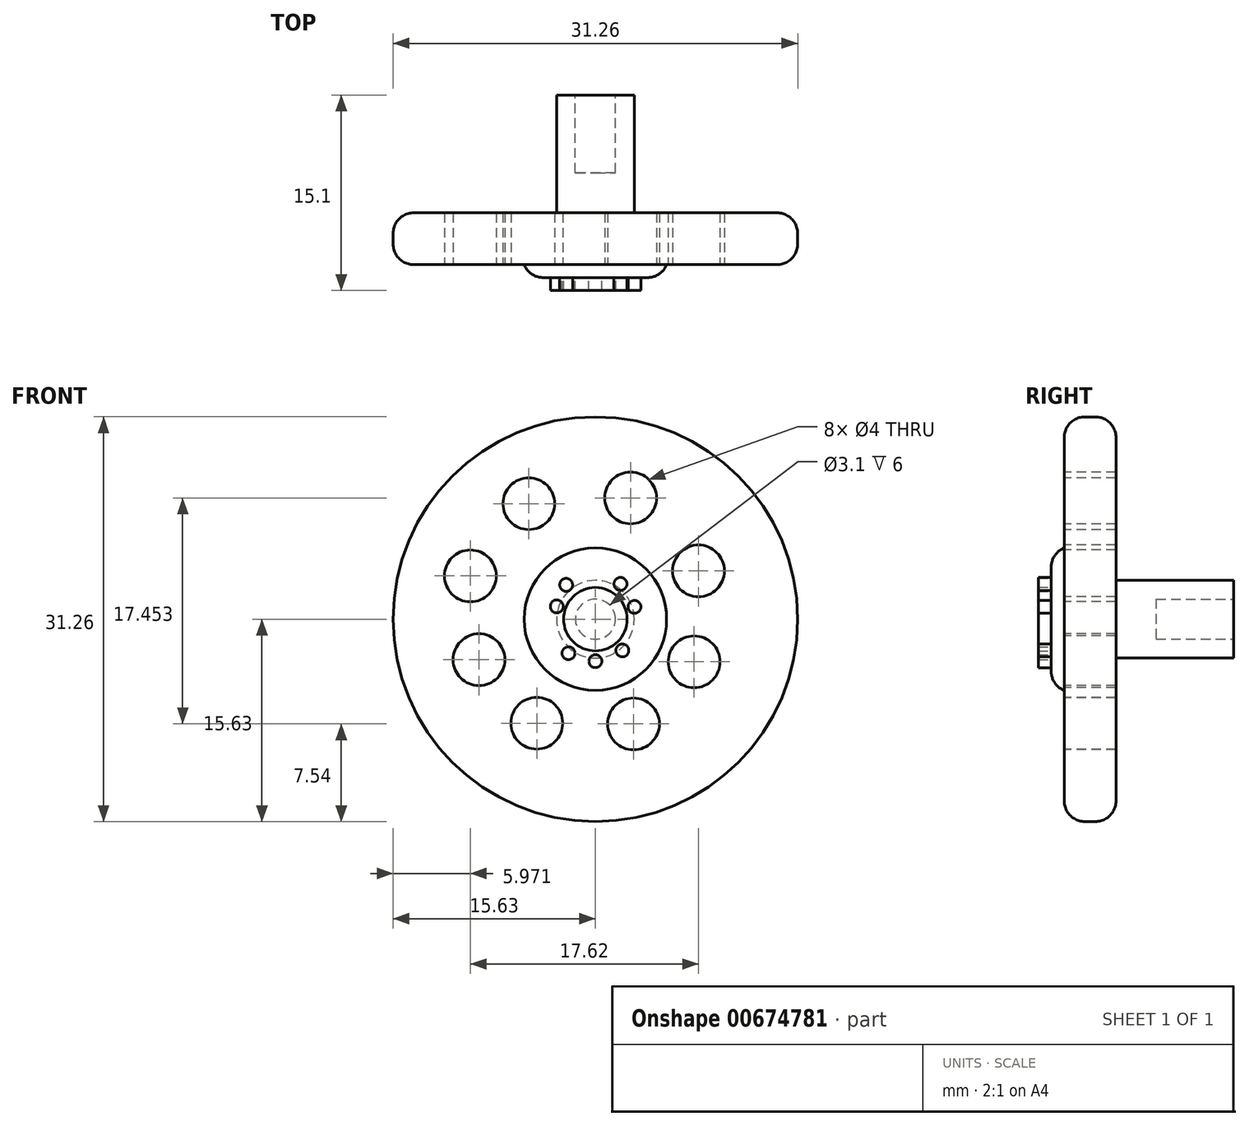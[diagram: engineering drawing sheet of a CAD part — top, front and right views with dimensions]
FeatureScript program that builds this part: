
annotation { "Feature Type Name" : "Feature", "Feature Type Description" : "" }
export const myFeature = defineFeature(function(context is Context, id is Id, definition is map)
    precondition{}
    {
        {
            var Q0;
            Q0=qCreatedBy(makeId("Front.planeOp"),FACE);
            var sketch = newSketch(context, id + "F0", { "sketchPlane" : qUnion([Q0])});
            skCircle(sketch, "E0", {"center": v(0, 0) * mm, "radius": 15.62 * mm});
            skSolve(sketch);
        }
        {
            var Q0;
            Q0=makeQuery(id+"F0.imprint","IMPRINT",FACE,{"disambiguationData":[TD([[makeQuery(id+"F0.imprint","IMPRINT",EDGE,{"derivedFrom":sQuery(id+"F0.wireOp",EDGE,"E0")}),1.0]])]});
            extrude(context, id + "F1", {"entities" : qUnion([Q0]), "depth" : 4 * mm, "offsetDistance" : 25.4 * mm});
        }
        {
            var Q0;
            Q0=makeQuery(id+"F1.opExtrude","CAP_FACE",FACE,{"disambiguationData":[OSD([sQuery(id+"F0.wireOp",EDGE,"E0")])],"isStart":false});
            var sketch = newSketch(context, id + "F2", { "sketchPlane" : qUnion([Q0])});
            skCircle(sketch, "E1", {"center": v(0, 0) * mm, "radius": 2.45 * mm});
            skSolve(sketch);
        }
        {
            var Q0;
            Q0=makeQuery(id+"F2.imprint","IMPRINT",FACE,{"disambiguationData":[TD([[makeQuery(id+"F2.imprint","IMPRINT",EDGE,{"derivedFrom":sQuery(id+"F2.wireOp",EDGE,"E1")}),1.0]])]});
            extrude(context, id + "F3", {"entities" : qUnion([Q0]), "operationType" : NewBodyOperationType.ADD, "depth" : 2 * mm, "offsetDistance" : 25.4 * mm});
        }
        {
            var Q0;
            Q0=makeQuery(id+"F1.opExtrude","CAP_FACE",FACE,{"disambiguationData":[OSD([sQuery(id+"F0.wireOp",EDGE,"E0")])],"isStart":true});
            var sketch = newSketch(context, id + "F4", { "sketchPlane" : qUnion([Q0])});
            skCircle(sketch, "E2", {"center": v(0, 0) * mm, "radius": 3 * mm});
            skSolve(sketch);
        }
        {
            var Q0;
            Q0 = qSketchRegion(id + "F4", true);
            extrude(context, id + "F5", {"entities" : qUnion([Q0]), "operationType" : NewBodyOperationType.ADD, "depth" : 9.1 * mm, "offsetDistance" : 25.4 * mm});
        }
        {
            var Q0;
            Q0=makeQuery(id+"F5.opExtrude","CAP_FACE",FACE,{"disambiguationData":[OSD([sQuery(id+"F4.wireOp",EDGE,"E2")])],"isStart":false});
            var sketch = newSketch(context, id + "F6", { "sketchPlane" : qUnion([Q0])});
            skCircle(sketch, "E3", {"center": v(0, 0) * mm, "radius": 1.55 * mm});
            skSolve(sketch);
        }
        {
            var Q0;
            Q0=makeQuery(id+"F6.imprint","IMPRINT",FACE,{"disambiguationData":[TD([[makeQuery(id+"F6.imprint","IMPRINT",EDGE,{"derivedFrom":sQuery(id+"F6.wireOp",EDGE,"E3")}),1.0]])]});
            extrude(context, id + "F7", {"entities" : qUnion([Q0]), "operationType" : NewBodyOperationType.REMOVE, "oppositeDirection" : true, "depth" : 6 * mm, "offsetDistance" : 25.4 * mm});
        }
        {
            var Q0;
            Q0=makeQuery(id+"F1.opExtrude","CAP_FACE",FACE,{"disambiguationData":[OSD([sQuery(id+"F0.wireOp",EDGE,"E0")])],"isStart":false});
            var sketch = newSketch(context, id + "F8", { "sketchPlane" : qUnion([Q0])});
            skCircle(sketch, "E4", {"center": v(0, 0) * mm, "radius": 5.5 * mm});
            skSolve(sketch);
        }
        {
            var Q0;
            Q0 = qSketchRegion(id + "F8", true);
            extrude(context, id + "F9", {"entities" : qUnion([Q0]), "operationType" : NewBodyOperationType.ADD, "depth" : 1 * mm, "offsetDistance" : 25.4 * mm});
        }
        {
            var Q0;
            Q0=makeQuery(id+"F1.opExtrude","CAP_EDGE",EDGE,{"disambiguationData":[OSD([sQuery(id+"F0.wireOp",EDGE,"E0")])],"isStart":false});
            var Q1;
            Q1=makeQuery(id+"F1.opExtrude","CAP_EDGE",EDGE,{"disambiguationData":[OSD([sQuery(id+"F0.wireOp",EDGE,"E0")])],"isStart":true});
            var Q2;
            Q2=makeQuery(id+"F9.opExtrude","CAP_EDGE",EDGE,{"disambiguationData":[OSD([sQuery(id+"F8.wireOp",EDGE,"E4")])],"isStart":false});
            fillet(context, id + "F10", {"entities" : qUnion([Q0, Q1, Q2]), "radius" : 1.59 * mm, "tangentPropagation" : true, "allowEdgeOverflow" : false});
        }
        {
            var Q0;
            Q0=makeQuery(id+"F9.opExtrude","CAP_FACE",FACE,{"disambiguationData":[OSD([sQuery(id+"F8.wireOp",EDGE,"E4")])],"isStart":false});
            var sketch = newSketch(context, id + "F11", { "sketchPlane" : qUnion([Q0])});
            skCircle(sketch, "E5", {"center": v(0, 3.12) * mm, "radius": 0.5 * mm});
            skCircle(sketch, "E6", {"center": v(-2.26, 2.65) * mm, "radius": 0.5 * mm});
            skCircle(sketch, "E7", {"center": v(-2.98, 0.99) * mm, "radius": 0.5 * mm});
            skCircle(sketch, "E8", {"center": v(1.94, 2.72) * mm, "radius": 0.5 * mm});
            skCircle(sketch, "E9", {"center": v(3.02, 0.95) * mm, "radius": 0.5 * mm});
            skCircle(sketch, "E10", {"center": v(-3.2, -0.9) * mm, "radius": 0.5 * mm});
            skCircle(sketch, "E11", {"center": v(3.02, -0.9) * mm, "radius": 0.5 * mm});
            skCircle(sketch, "E12", {"center": v(2.08, -2.41) * mm, "radius": 0.5 * mm});
            skCircle(sketch, "E13", {"center": v(-2.08, -2.63) * mm, "radius": 0.5 * mm});
            skCircle(sketch, "E14", {"center": v(0, -3.24) * mm, "radius": 0.5 * mm});
            skSolve(sketch);
        }
        {
            var Q0;
            Q0=makeQuery(id+"F11.imprint","IMPRINT",FACE,{"disambiguationData":[TD([[makeQuery(id+"F11.imprint","IMPRINT",EDGE,{"derivedFrom":sQuery(id+"F11.wireOp",EDGE,"E7")}),1.0]])]});
            var Q1;
            Q1=makeQuery(id+"F11.imprint","IMPRINT",FACE,{"disambiguationData":[TD([[makeQuery(id+"F11.imprint","IMPRINT",EDGE,{"derivedFrom":sQuery(id+"F11.wireOp",EDGE,"E6")}),1.0]])]});
            var Q2;
            Q2=makeQuery(id+"F11.imprint","IMPRINT",FACE,{"disambiguationData":[TD([[makeQuery(id+"F11.imprint","IMPRINT",EDGE,{"derivedFrom":sQuery(id+"F11.wireOp",EDGE,"E8")}),1.0]])]});
            var Q3;
            Q3=makeQuery(id+"F11.imprint","IMPRINT",FACE,{"disambiguationData":[TD([[makeQuery(id+"F11.imprint","IMPRINT",EDGE,{"derivedFrom":sQuery(id+"F11.wireOp",EDGE,"E9")}),1.0]])]});
            var Q4;
            Q4=makeQuery(id+"F11.imprint","IMPRINT",FACE,{"disambiguationData":[TD([[makeQuery(id+"F11.imprint","IMPRINT",EDGE,{"derivedFrom":sQuery(id+"F11.wireOp",EDGE,"E12")}),1.0]])]});
            var Q5;
            Q5=makeQuery(id+"F11.imprint","IMPRINT",FACE,{"disambiguationData":[TD([[makeQuery(id+"F11.imprint","IMPRINT",EDGE,{"derivedFrom":sQuery(id+"F11.wireOp",EDGE,"E14")}),1.0]])]});
            var Q6;
            Q6=makeQuery(id+"F11.imprint","IMPRINT",FACE,{"disambiguationData":[TD([[makeQuery(id+"F11.imprint","IMPRINT",EDGE,{"derivedFrom":sQuery(id+"F11.wireOp",EDGE,"E13")}),1.0]])]});
            extrude(context, id + "F12", {"entities" : qUnion([Q0, Q1, Q2, Q3, Q4, Q5, Q6]), "operationType" : NewBodyOperationType.ADD, "depth" : 1 * mm, "offsetDistance" : 25.4 * mm});
        }
        {
            var Q0;
            Q0=makeQuery(id+"F1.opExtrude","CAP_FACE",FACE,{"disambiguationData":[OSD([sQuery(id+"F0.wireOp",EDGE,"E0")])],"isStart":false});
            var sketch = newSketch(context, id + "F13", { "sketchPlane" : qUnion([Q0])});
            skCircle(sketch, "E15", {"center": v(-5.14, 8.92) * mm, "radius": 2 * mm});
            skCircle(sketch, "E16", {"center": v(-9.66, 3.34) * mm, "radius": 2 * mm});
            skCircle(sketch, "E17", {"center": v(-8.99, -3.13) * mm, "radius": 2 * mm});
            skCircle(sketch, "E18", {"center": v(-4.53, -8.03) * mm, "radius": 2 * mm});
            skCircle(sketch, "E19", {"center": v(2.94, -8.1) * mm, "radius": 2 * mm});
            skCircle(sketch, "E20", {"center": v(7.63, -3.3) * mm, "radius": 2 * mm});
            skCircle(sketch, "E21", {"center": v(7.96, 3.73) * mm, "radius": 2 * mm});
            skCircle(sketch, "E22", {"center": v(2.72, 9.36) * mm, "radius": 2 * mm});
            skSolve(sketch);
        }
        {
            var Q0;
            Q0=makeQuery(id+"F13.imprint","IMPRINT",FACE,{"disambiguationData":[TD([[makeQuery(id+"F13.imprint","IMPRINT",EDGE,{"derivedFrom":sQuery(id+"F13.wireOp",EDGE,"E15")}),1.0]])]});
            var Q1;
            Q1=makeQuery(id+"F13.imprint","IMPRINT",FACE,{"disambiguationData":[TD([[makeQuery(id+"F13.imprint","IMPRINT",EDGE,{"derivedFrom":sQuery(id+"F13.wireOp",EDGE,"E22")}),1.0]])]});
            var Q2;
            Q2=makeQuery(id+"F13.imprint","IMPRINT",FACE,{"disambiguationData":[TD([[makeQuery(id+"F13.imprint","IMPRINT",EDGE,{"derivedFrom":sQuery(id+"F13.wireOp",EDGE,"E21")}),1.0]])]});
            var Q3;
            Q3=makeQuery(id+"F13.imprint","IMPRINT",FACE,{"disambiguationData":[TD([[makeQuery(id+"F13.imprint","IMPRINT",EDGE,{"derivedFrom":sQuery(id+"F13.wireOp",EDGE,"E20")}),1.0]])]});
            var Q4;
            Q4=makeQuery(id+"F13.imprint","IMPRINT",FACE,{"disambiguationData":[TD([[makeQuery(id+"F13.imprint","IMPRINT",EDGE,{"derivedFrom":sQuery(id+"F13.wireOp",EDGE,"E19")}),1.0]])]});
            var Q5;
            Q5=makeQuery(id+"F13.imprint","IMPRINT",FACE,{"disambiguationData":[TD([[makeQuery(id+"F13.imprint","IMPRINT",EDGE,{"derivedFrom":sQuery(id+"F13.wireOp",EDGE,"E18")}),1.0]])]});
            var Q6;
            Q6=makeQuery(id+"F13.imprint","IMPRINT",FACE,{"disambiguationData":[TD([[makeQuery(id+"F13.imprint","IMPRINT",EDGE,{"derivedFrom":sQuery(id+"F13.wireOp",EDGE,"E17")}),1.0]])]});
            var Q7;
            Q7=makeQuery(id+"F13.imprint","IMPRINT",FACE,{"disambiguationData":[TD([[makeQuery(id+"F13.imprint","IMPRINT",EDGE,{"derivedFrom":sQuery(id+"F13.wireOp",EDGE,"E16")}),1.0]])]});
            extrude(context, id + "F14", {"entities" : qUnion([Q0, Q1, Q2, Q3, Q4, Q5, Q6, Q7]), "operationType" : NewBodyOperationType.REMOVE, "oppositeDirection" : true, "depth" : 25.4 * mm, "offsetDistance" : 25.4 * mm});
        }
    });
